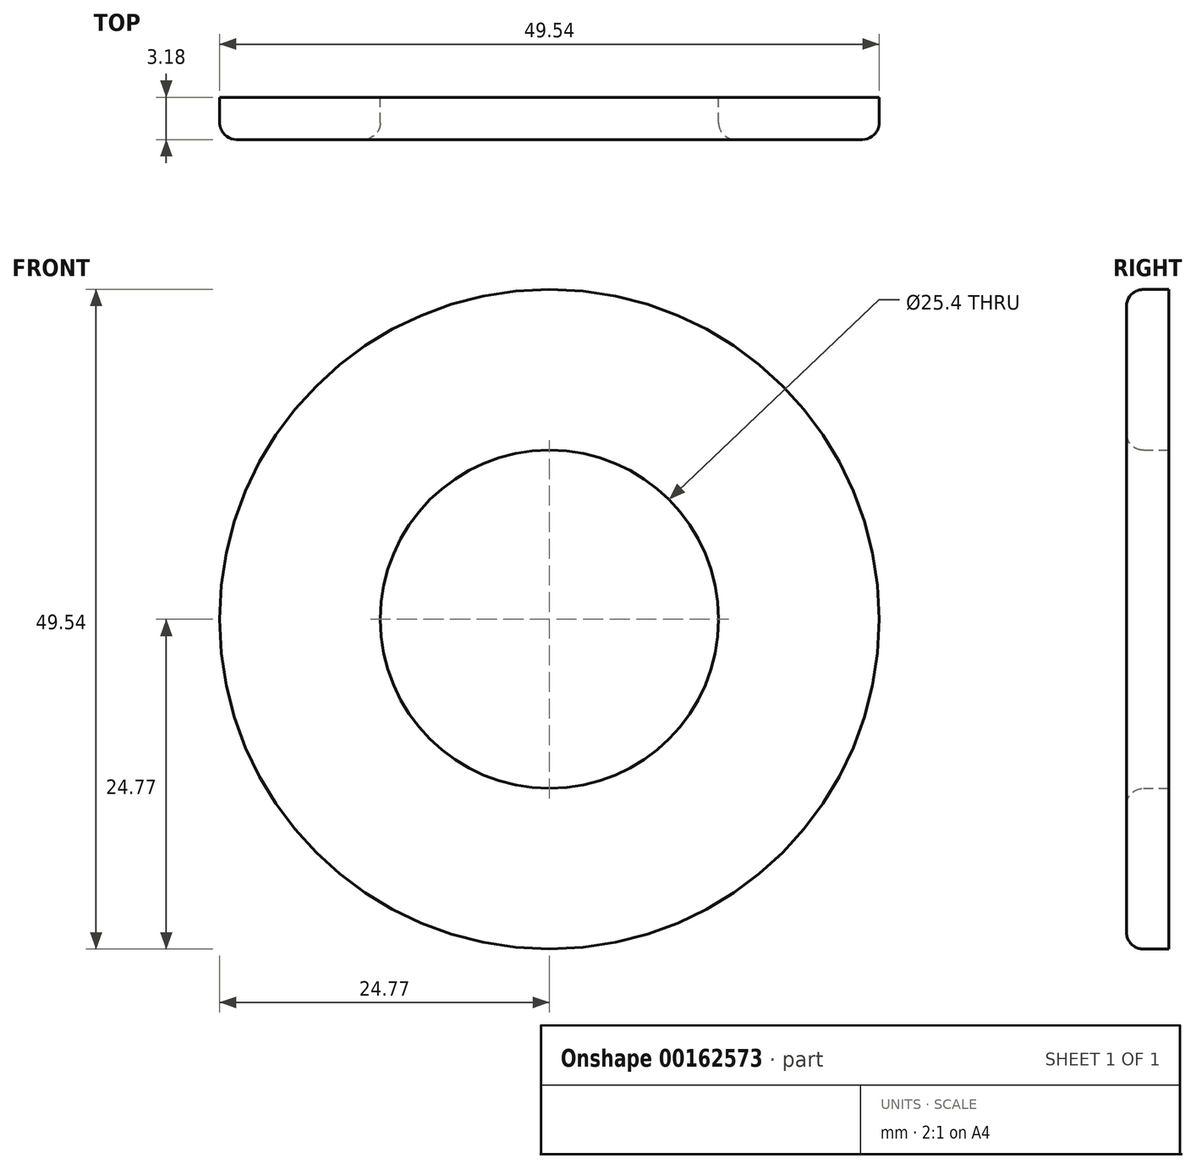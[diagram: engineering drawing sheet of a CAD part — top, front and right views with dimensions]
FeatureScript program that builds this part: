
annotation { "Feature Type Name" : "Feature", "Feature Type Description" : "" }
export const myFeature = defineFeature(function(context is Context, id is Id, definition is map)
    precondition{}
    {
        {
            var Q0;
            Q0=qCreatedBy(makeId("Front.planeOp"),FACE);
            var sketch = newSketch(context, id + "F0", { "sketchPlane" : qUnion([Q0])});
            skCircle(sketch, "E0", {"center": v(0, 0) * mm, "radius": 24.77 * mm});
            skCircle(sketch, "E1", {"center": v(0, 0) * mm, "radius": 12.7 * mm});
            skSolve(sketch);
        }
        {
            var Q0;
            Q0 = qSketchRegion(id + "F0", true);
            extrude(context, id + "F2", {"entities" : qUnion([Q0]), "depth" : 3.17 * mm});
        }
        {
            var Q0;
            Q0=makeQuery(id+"F2.opExtrude","CAP_EDGE",EDGE,{"disambiguationData":[OSD([sQuery(id+"F0.wireOp",EDGE,"E1")])],"isStart":false});
            var Q1;
            Q1=makeQuery(id+"F2.opExtrude","CAP_EDGE",EDGE,{"disambiguationData":[OSD([sQuery(id+"F0.wireOp",EDGE,"E0")])],"isStart":false});
            fillet(context, id + "F1", {"entities" : qUnion([Q0, Q1]), "radius" : 1.27 * mm, "tangentPropagation" : true, "allowEdgeOverflow" : false});
        }
    });
